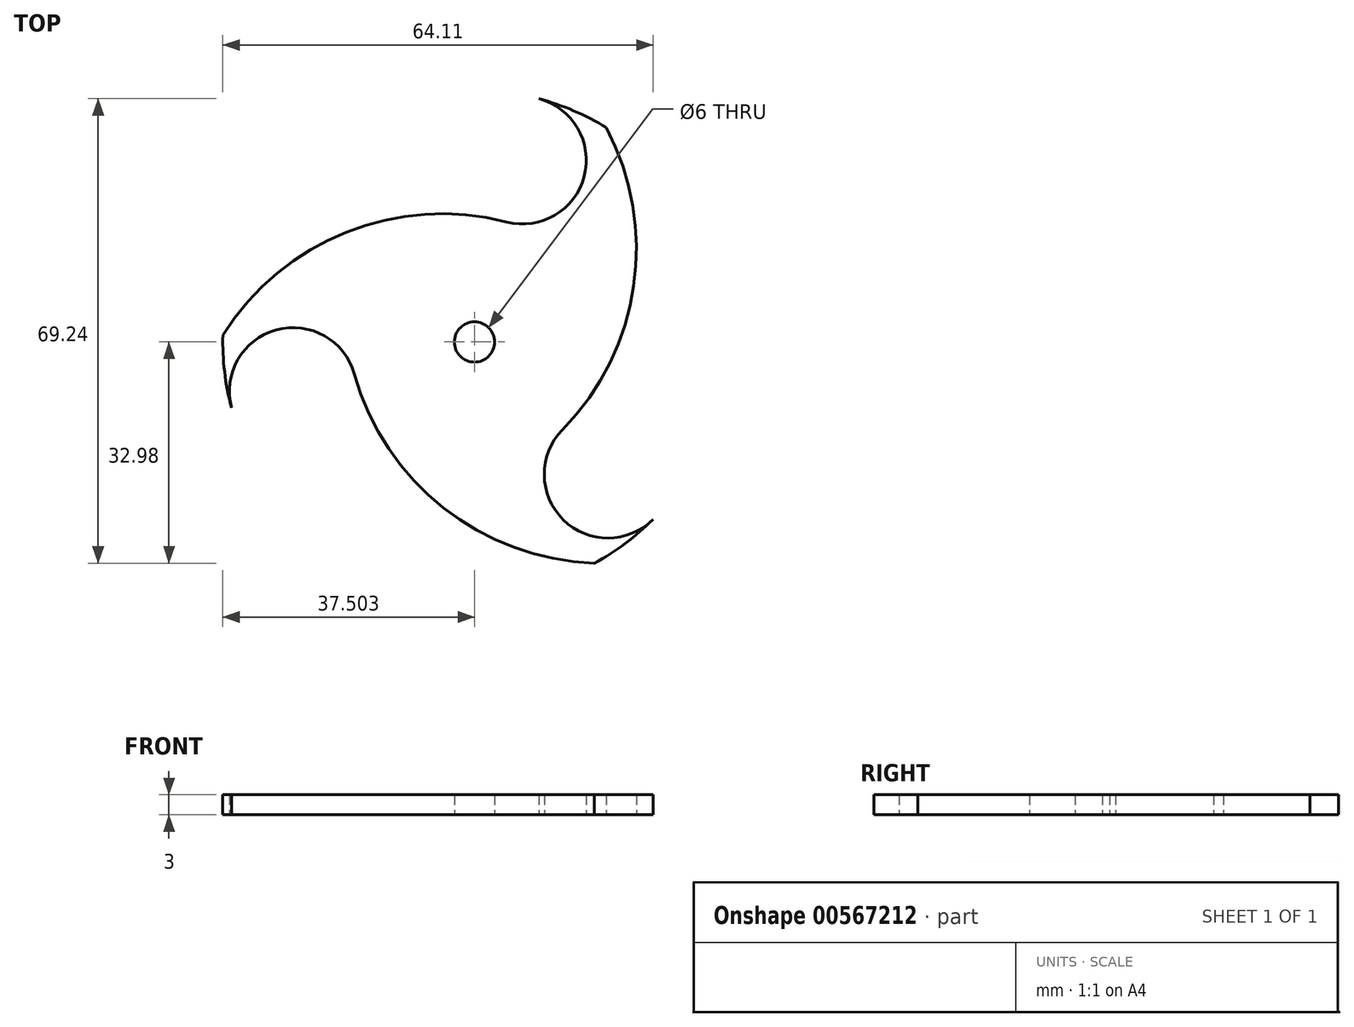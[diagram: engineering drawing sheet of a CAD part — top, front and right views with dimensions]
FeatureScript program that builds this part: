
annotation { "Feature Type Name" : "Feature", "Feature Type Description" : "" }
export const myFeature = defineFeature(function(context is Context, id is Id, definition is map)
    precondition{}
    {
        {
            var Q0;
            Q0=qCreatedBy(makeId("Top.planeOp"),FACE);
            var sketch = newSketch(context, id + "F0", { "sketchPlane" : qUnion([Q0])});
            skLineSegment(sketch, "E0.bottom", {"start": v(-29.85, 45.37) * mm, "end": v(45.15, 45.37) * mm, "construction": true});
            skLineSegment(sketch, "E0.top", {"start": v(-29.85, -29.63) * mm, "end": v(45.15, -29.63) * mm, "construction": true});
            skLineSegment(sketch, "E0.left", {"start": v(-29.85, 45.37) * mm, "end": v(-29.85, -29.63) * mm, "construction": true});
            skLineSegment(sketch, "E0.right", {"start": v(45.15, 45.37) * mm, "end": v(45.15, -29.63) * mm, "construction": true});
            skLineSegment(sketch, "E1", {"start": v(-29.85, 45.37) * mm, "end": v(45.15, -29.63) * mm, "construction": true});
            skCircle(sketch, "E2", {"center": v(7.65, 7.87) * mm, "radius": 3 * mm});
            skCircle(sketch, "E3", {"center": v(7.65, 7.87) * mm, "radius": 37.5 * mm});
            skArc(sketch, "E4", {"start": v(20.75, -5.23) * mm, "mid": v(31.37, 16.23) * mm, "end": v(27.3, 39.81) * mm});
            skArc(sketch, "E5", {"start": v(20.75, -5.23) * mm, "mid": v(20.87, -18.62) * mm, "end": v(34.26, -18.55) * mm});
            skArc(sketch, "E6.1.0", {"start": v(12.45, 25.77) * mm, "mid": v(-11.44, 24.23) * mm, "end": v(-29.83, 8.9) * mm});
            skArc(sketch, "E6.1.1", {"start": v(12.45, 25.77) * mm, "mid": v(23.99, 32.56) * mm, "end": v(17.23, 44.13) * mm});
            skArc(sketch, "E6.2.0", {"start": v(-10.24, 3.07) * mm, "mid": v(3.03, -16.85) * mm, "end": v(25.5, -25.11) * mm});
            skArc(sketch, "E6.2.1", {"start": v(-10.24, 3.07) * mm, "mid": v(-21.9, 9.67) * mm, "end": v(-28.53, -1.96) * mm});
            skSolve(sketch);
        }
        {
            var Q0;
            Q0=makeQuery(id+"F0.imprint","IMPRINT",FACE,{"disambiguationData":[TD([[makeQuery(id+"F0.imprint","IMPRINT",EDGE,{"derivedFrom":sQuery(id+"F0.wireOp",EDGE,"E2")}),-1.0]])]});
            extrude(context, id + "F1", {"entities" : qUnion([Q0]), "depth" : 3 * mm, "offsetDistance" : 25 * mm});
        }
    });
